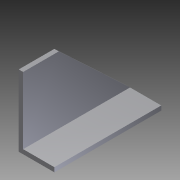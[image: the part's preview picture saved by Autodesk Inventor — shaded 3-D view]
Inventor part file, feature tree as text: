
AUTODESK INVENTOR PART (.ipt)
format: ipt  version: 2012 (Build 160160000, 160)  size: 76,800 bytes
history: native  units: in
note: dims shown in document units (in); Inventor stores cm internally (conversion verified against a paired STEP export)
features: other x3, sketch x2
ambient origin geometry x8: Origin, YZ Plane, XZ Plane, XY Plane, X Axis, Y Axis, Z Axis, Center Point
bodies: Solid1 (feature_tree)
feature tree (5):
  other  "manipulator corner brace.ipt"
  other  "Solid1::manipulator corner brace.ipt"
  sketch  "Sketch1"  dims[d0=0.3937in]
  sketch  "Sketch2"
  other  "TaggingFeature1"
